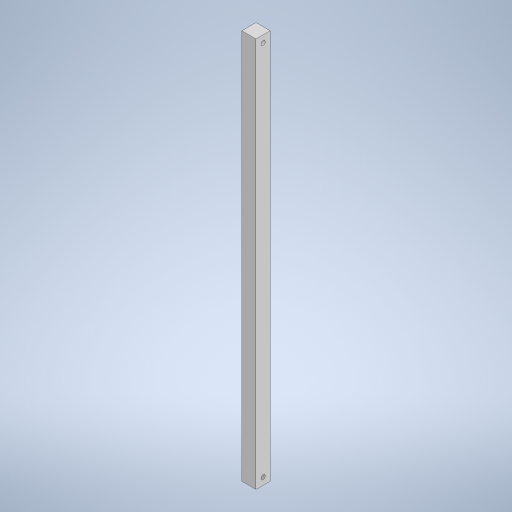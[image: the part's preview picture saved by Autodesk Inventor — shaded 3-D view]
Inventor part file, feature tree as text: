
AUTODESK INVENTOR PART (.ipt)
format: ipt  version: 2023 (Build 270158000, 158)  size: 243,712 bytes
history: native  units: mm
features: sketch x2, other x1, extrude x1, hole x1
ambient origin geometry x8: Origin, YZ Plane, XZ Plane, XY Plane, X Axis, Y Axis, Z Axis, Center Point
bodies: Body1 (feature_tree)
feature tree (5):
  other  "ソリッド1"
  extrude  "押し出し1"  Depth=10.0mm
  hole  "穴1"  [1 undecoded]
  sketch  "スケッチ1"
  sketch  "スケッチ2"
note: 1 required parameter value undecoded (feature->parameter linkage not recoverable at this tier; creation-order binding heuristic only, values carry confidence <= 0.55)
